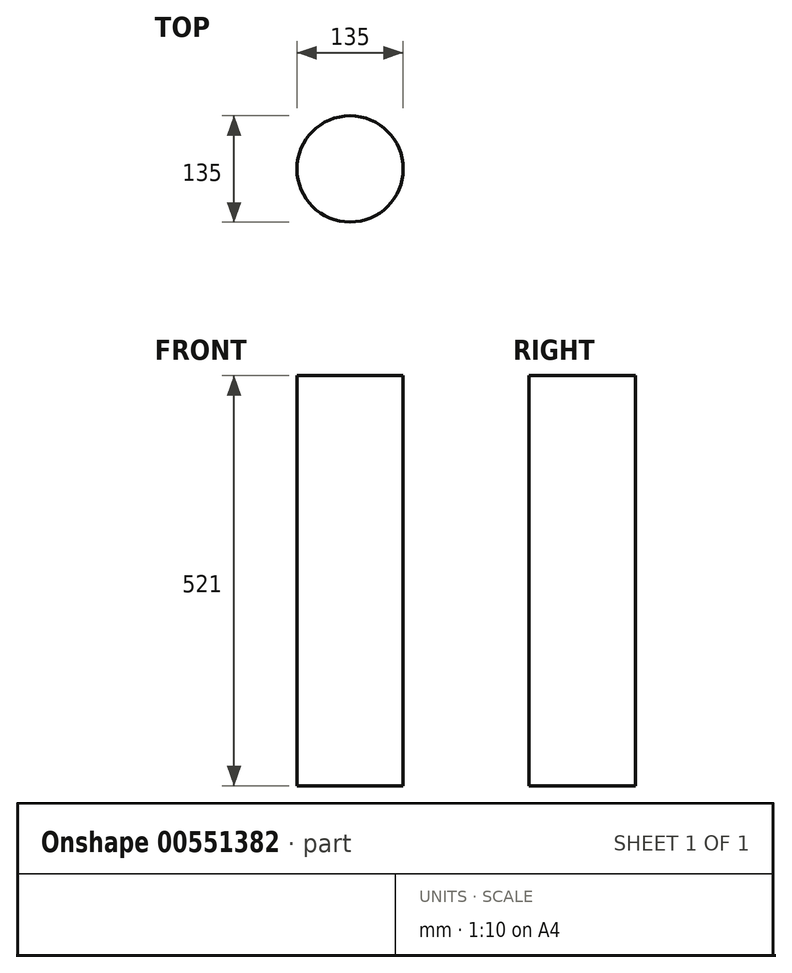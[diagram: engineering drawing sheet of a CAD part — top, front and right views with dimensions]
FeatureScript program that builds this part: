
annotation { "Feature Type Name" : "Feature", "Feature Type Description" : "" }
export const myFeature = defineFeature(function(context is Context, id is Id, definition is map)
    precondition{}
    {
        {
            var Q0;
            Q0=qCreatedBy(makeId("Top.planeOp"),FACE);
            var sketch = newSketch(context, id + "F0", { "sketchPlane" : qUnion([Q0])});
            skCircle(sketch, "E0", {"center": v(0, 0) * mm, "radius": 67.5 * mm});
            skSolve(sketch);
        }
        {
            var Q0;
            Q0=makeQuery(id+"F0.imprint","IMPRINT",FACE,{"disambiguationData":[TD([[makeQuery(id+"F0.imprint","IMPRINT",EDGE,{"derivedFrom":sQuery(id+"F0.wireOp",EDGE,"E0")}),1.0]])]});
            extrude(context, id + "F1", {"entities" : qUnion([Q0]), "depth" : 521 * mm, "offsetDistance" : 25 * mm});
        }
    });
